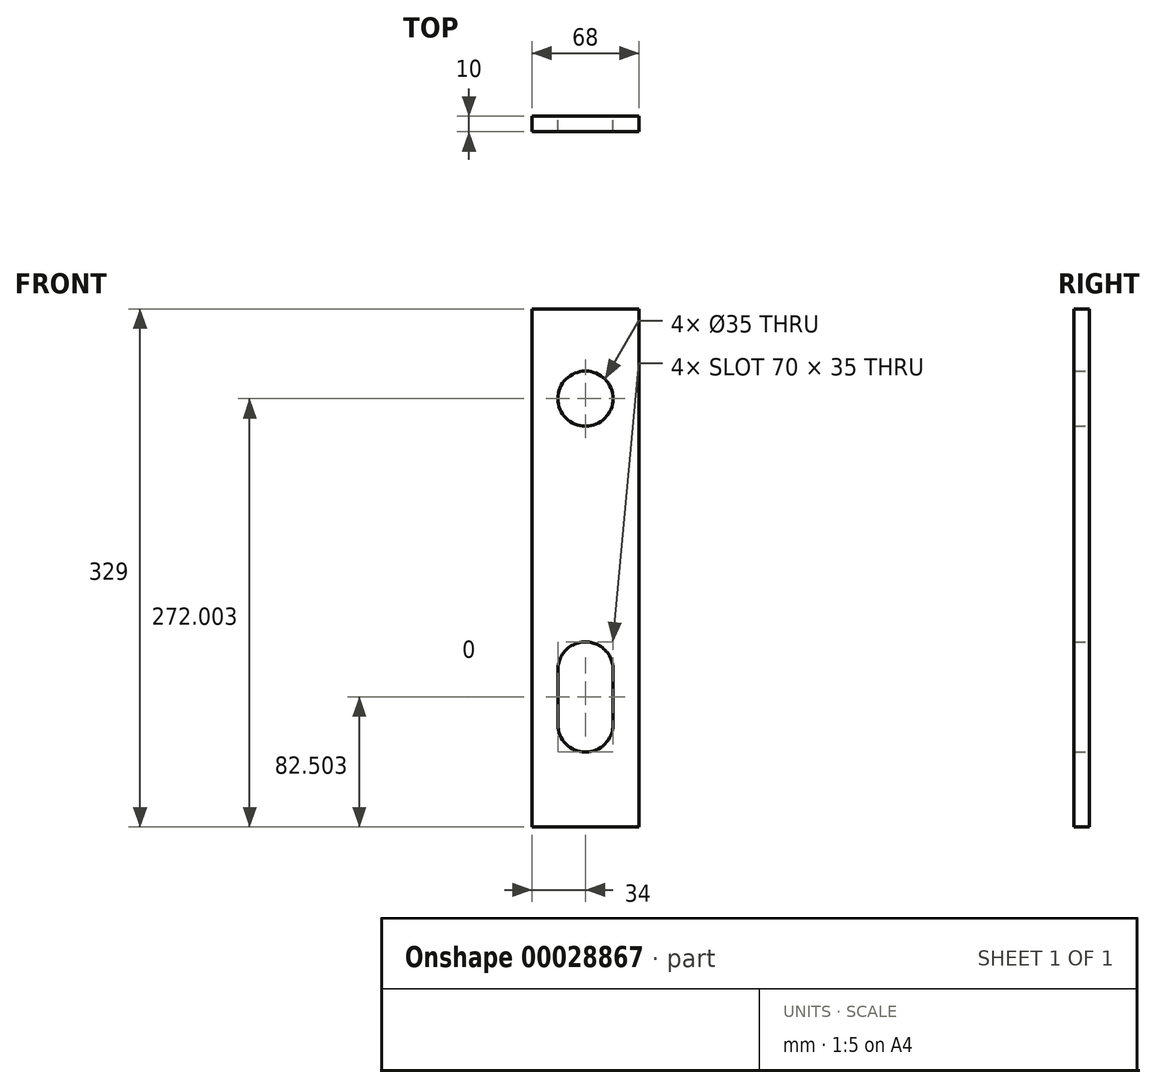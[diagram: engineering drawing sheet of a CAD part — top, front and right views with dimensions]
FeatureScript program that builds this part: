
annotation { "Feature Type Name" : "Feature", "Feature Type Description" : "" }
export const myFeature = defineFeature(function(context is Context, id is Id, definition is map)
    precondition{}
    {
        {
            var Q0;
            Q0=qCreatedBy(makeId("Front.planeOp"),FACE);
            var sketch = newSketch(context, id + "F0", { "sketchPlane" : qUnion([Q0])});
            skLineSegment(sketch, "E0.bottom", {"start": v(-68, 312.16) * mm, "end": v(0, 312.16) * mm});
            skLineSegment(sketch, "E0.top", {"start": v(-68, -16.84) * mm, "end": v(0, -16.84) * mm});
            skLineSegment(sketch, "E0.left", {"start": v(-68, 312.16) * mm, "end": v(-68, -16.84) * mm});
            skLineSegment(sketch, "E0.right", {"start": v(0, 312.16) * mm, "end": v(0, -16.84) * mm});
            skCircle(sketch, "E1", {"center": v(-34, 255.16) * mm, "radius": 17.5 * mm});
            skCircle(sketch, "E2", {"center": v(-34, 48.16) * mm, "radius": 17.5 * mm});
            skCircle(sketch, "E3", {"center": v(-34, 83.16) * mm, "radius": 17.5 * mm});
            skLineSegment(sketch, "E4", {"start": v(-16.5, 83.16) * mm, "end": v(-16.5, 48.16) * mm});
            skLineSegment(sketch, "E5", {"start": v(-51.5, 83.21) * mm, "end": v(-51.5, 48.16) * mm});
            skSolve(sketch);
        }
        {
            var Q0;
            Q0=makeQuery(id+"F0.imprint","IMPRINT",FACE,{"disambiguationData":[TD([[makeQuery(id+"F0.imprint","IMPRINT",EDGE,{"derivedFrom":sQuery(id+"F0.wireOp",EDGE,"E0.bottom")}),-1.0]])]});
            extrude(context, id + "F1", {"entities" : qUnion([Q0]), "depth" : 10 * mm});
        }
    });
